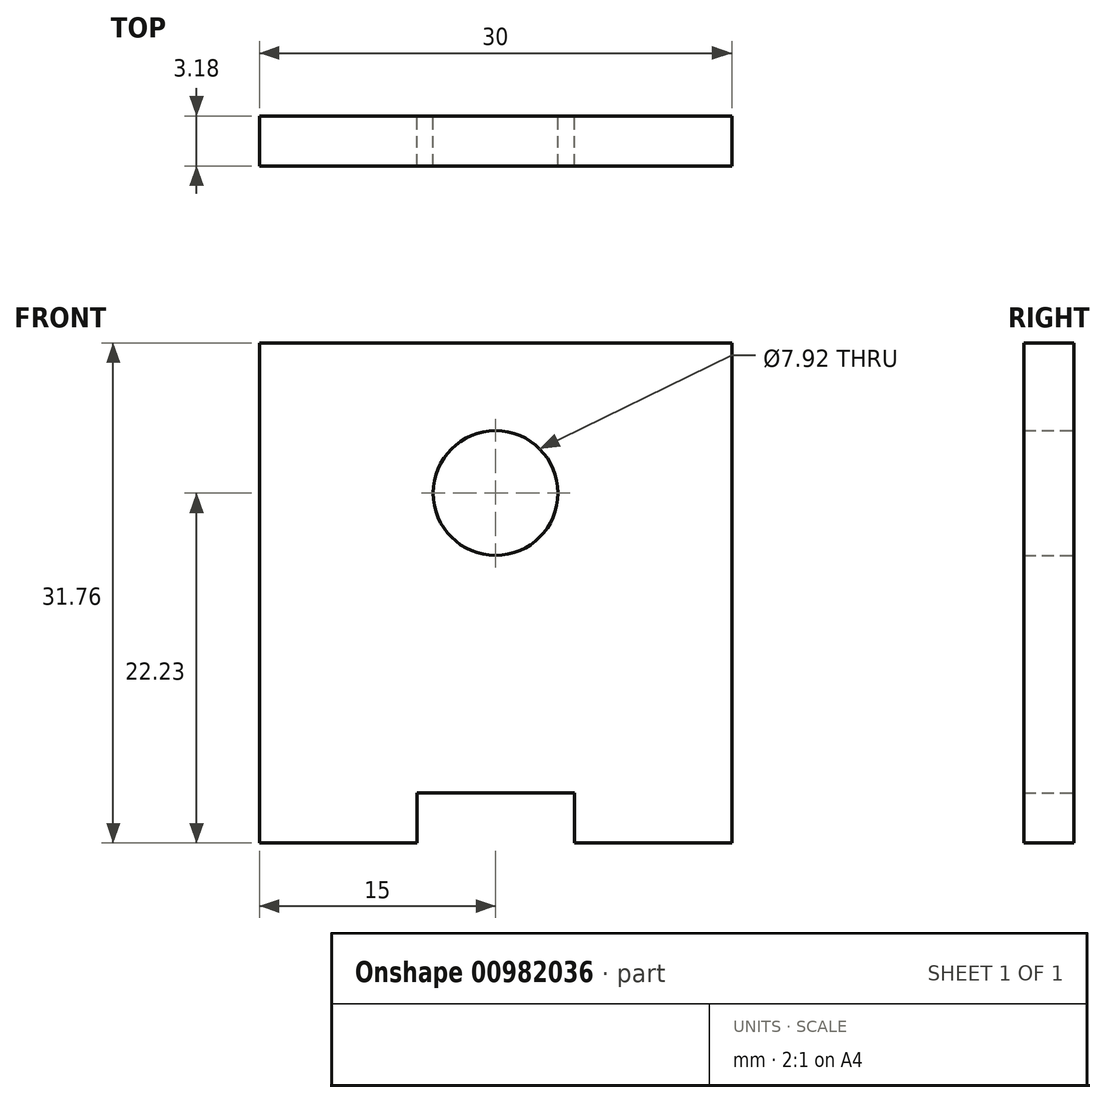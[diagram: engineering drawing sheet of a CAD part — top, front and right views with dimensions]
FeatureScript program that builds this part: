
annotation { "Feature Type Name" : "Feature", "Feature Type Description" : "" }
export const myFeature = defineFeature(function(context is Context, id is Id, definition is map)
    precondition{}
    {
        {
            var Q0;
            Q0=qCreatedBy(makeId("Front.planeOp"),FACE);
            var sketch = newSketch(context, id + "F0", { "sketchPlane" : qUnion([Q0])});
            skLineSegment(sketch, "E0.top", {"start": v(15, 15.88) * mm, "end": v(-15, 15.87) * mm});
            skLineSegment(sketch, "E0.left", {"start": v(15, -15.87) * mm, "end": v(15, 15.88) * mm});
            skLineSegment(sketch, "E0.right", {"start": v(-15, -15.88) * mm, "end": v(-15, 15.88) * mm});
            skPoint(sketch, "E0.middle", {"position": v(0, 0) * mm});
            skCircle(sketch, "E1", {"center": v(0, 6.35) * mm, "radius": 3.96 * mm});
            skLineSegment(sketch, "E2", {"start": v(-15, -15.88) * mm, "end": v(-5, -15.87) * mm});
            skLineSegment(sketch, "E3", {"start": v(-5, -15.87) * mm, "end": v(-5, -12.7) * mm});
            skLineSegment(sketch, "E4", {"start": v(-5, -12.7) * mm, "end": v(5, -12.7) * mm});
            skLineSegment(sketch, "E5", {"start": v(5, -12.7) * mm, "end": v(5, -15.87) * mm});
            skLineSegment(sketch, "E6", {"start": v(5, -15.87) * mm, "end": v(15, -15.87) * mm});
            skSolve(sketch);
        }
        {
            var Q0;
            Q0 = qSketchRegion(id + "F0", true);
            extrude(context, id + "F1", {"entities" : qUnion([Q0]), "depth" : 3.17 * mm, "offsetDistance" : 25 * mm});
        }
    });
